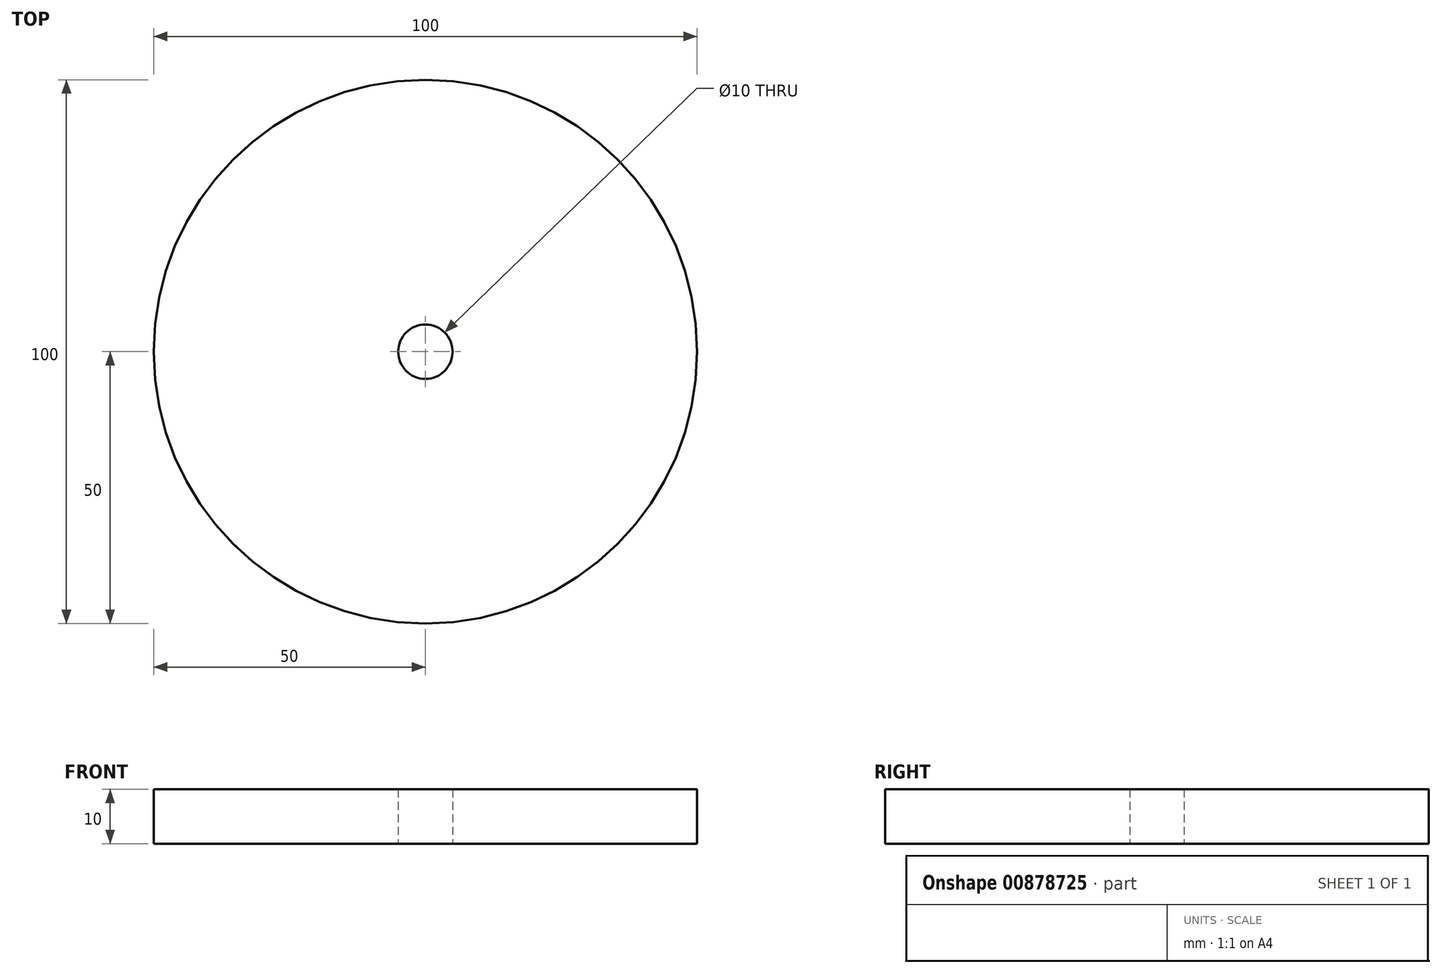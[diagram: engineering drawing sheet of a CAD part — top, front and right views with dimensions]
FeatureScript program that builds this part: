
annotation { "Feature Type Name" : "Feature", "Feature Type Description" : "" }
export const myFeature = defineFeature(function(context is Context, id is Id, definition is map)
    precondition{}
    {
        {
            var Q0;
            Q0=qCreatedBy(makeId("Top.planeOp"),FACE);
            var sketch = newSketch(context, id + "F0", { "sketchPlane" : qUnion([Q0])});
            skCircle(sketch, "E0", {"center": v(0, 0) * mm, "radius": 5 * mm});
            skCircle(sketch, "E1", {"center": v(0, 0) * mm, "radius": 50 * mm});
            skSolve(sketch);
        }
        {
            var Q0;
            Q0 = qSketchRegion(id + "F0", true);
            extrude(context, id + "F1", {"entities" : qUnion([Q0]), "depth" : 10 * mm, "offsetDistance" : 25 * mm});
        }
    });
